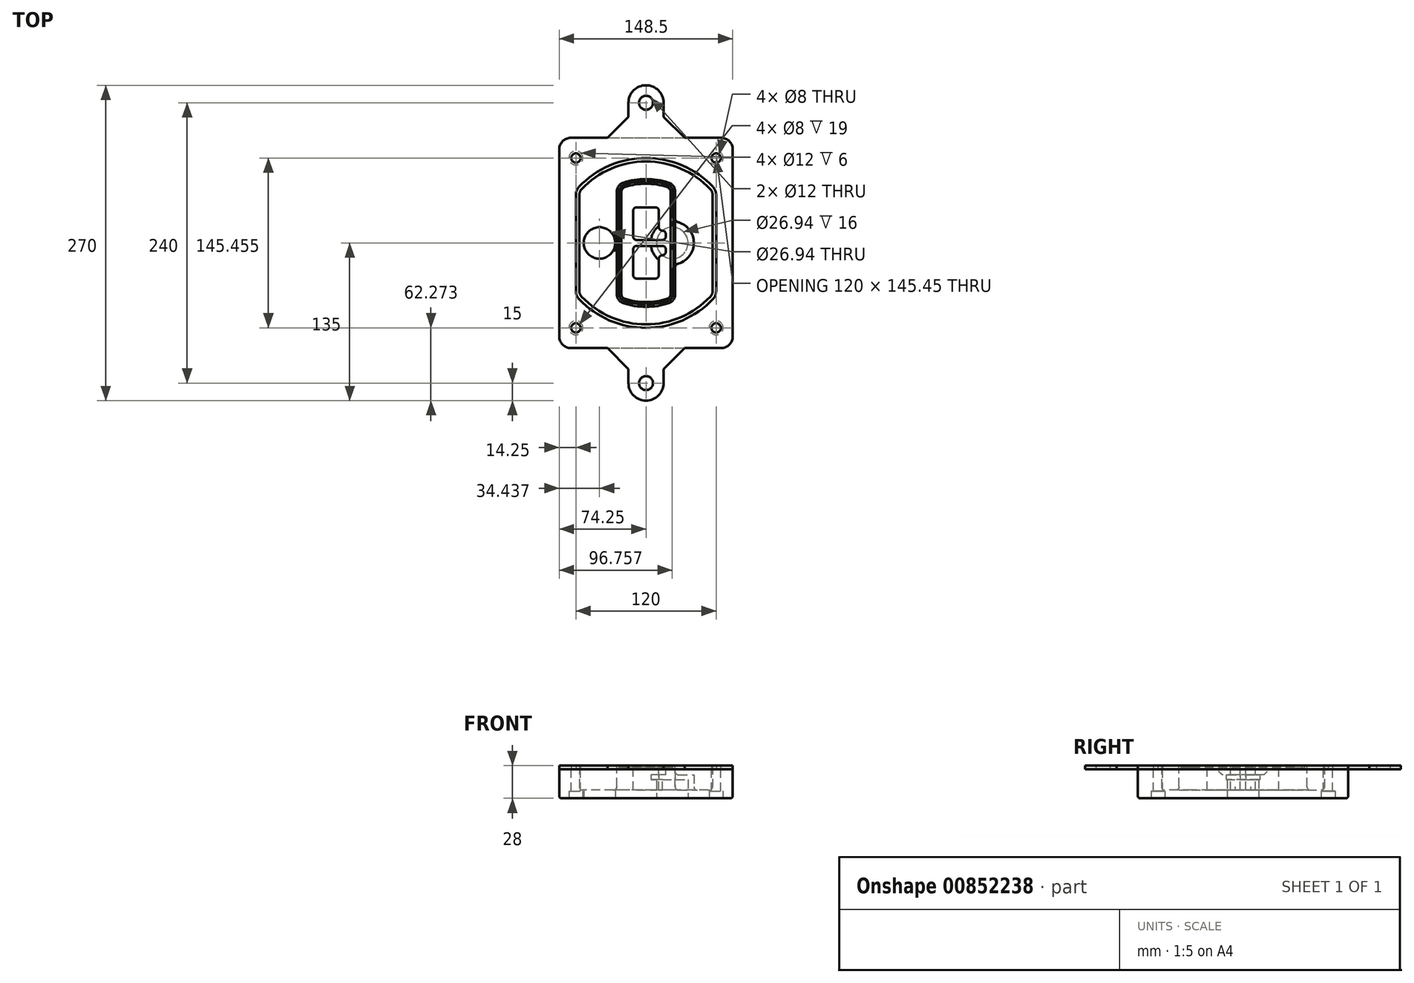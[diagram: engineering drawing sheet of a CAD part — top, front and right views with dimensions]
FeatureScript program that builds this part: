
annotation { "Feature Type Name" : "Feature", "Feature Type Description" : "" }
export const myFeature = defineFeature(function(context is Context, id is Id, definition is map)
    precondition{}
    {
        {
            var Q0;
            Q0=qCreatedBy(makeId("Top.planeOp"),FACE);
            var sketch = newSketch(context, id + "F0", { "sketchPlane" : qUnion([Q0])});
            skPoint(sketch, "E0.rect.middle", {"position": v(0, 0) * mm});
            skLineSegment(sketch, "E1.bottom", {"start": v(-64.25, -90) * mm, "end": v(64.25, -90) * mm});
            skLineSegment(sketch, "E1.top", {"start": v(-64.25, 90) * mm, "end": v(64.25, 90) * mm});
            skLineSegment(sketch, "E1.left", {"start": v(-74.25, -80) * mm, "end": v(-74.25, 80) * mm});
            skLineSegment(sketch, "E1.right", {"start": v(74.25, -80) * mm, "end": v(74.25, 80) * mm});
            skLineSegment(sketch, "E2", {"start": v(-74.25, 90) * mm, "end": v(74.25, -90) * mm, "construction": true});
            skLineSegment(sketch, "E3", {"start": v(74.25, 90) * mm, "end": v(-74.25, -90) * mm, "construction": true});
            skCircle(sketch, "E4", {"center": v(-60, 72.73) * mm, "radius": 4 * mm});
            skCircle(sketch, "E5", {"center": v(60, 72.73) * mm, "radius": 4 * mm});
            skCircle(sketch, "E6", {"center": v(60, -72.73) * mm, "radius": 4 * mm});
            skCircle(sketch, "E7", {"center": v(-60, -72.73) * mm, "radius": 4 * mm});
            skLineSegment(sketch, "E8", {"start": v(-60, 72.73) * mm, "end": v(60, 72.73) * mm, "construction": true});
            skLineSegment(sketch, "E9", {"start": v(60, 72.73) * mm, "end": v(60, -72.73) * mm, "construction": true});
            skLineSegment(sketch, "E10", {"start": v(60, -72.73) * mm, "end": v(-60, -72.73) * mm, "construction": true});
            skLineSegment(sketch, "E11", {"start": v(-60, -72.73) * mm, "end": v(-60, 72.73) * mm, "construction": true});
            skLineSegment(sketch, "E12", {"start": v(-60, 41.18) * mm, "end": v(-60, -41.18) * mm});
            skLineSegment(sketch, "E13", {"start": v(60, 41.18) * mm, "end": v(60, -41.18) * mm});
            skArc(sketch, "E14", {"start": v(57.27, 48.05) * mm, "mid": v(0, 72.73) * mm, "end": v(-57.27, 48.05) * mm});
            skArc(sketch, "E15", {"start": v(-57.27, -48.05) * mm, "mid": v(0, -72.73) * mm, "end": v(57.27, -48.05) * mm});
            skLineSegment(sketch, "E16", {"start": v(-60, 0) * mm, "end": v(60, 0) * mm, "construction": true});
            skPoint(sketch, "E17.visualSharp", {"position": v(-60, -45) * mm});
            skArc(sketch, "E17.filletArc", {"start": v(-60, -41.18) * mm, "mid": v(-59.3, -44.87) * mm, "end": v(-57.27, -48.05) * mm});
            skPoint(sketch, "E18.visualSharp", {"position": v(-60, 45) * mm});
            skArc(sketch, "E18.filletArc", {"start": v(-57.27, 48.05) * mm, "mid": v(-59.3, 44.87) * mm, "end": v(-60, 41.18) * mm});
            skPoint(sketch, "E19.visualSharp", {"position": v(60, 45) * mm});
            skArc(sketch, "E19.filletArc", {"start": v(60, 41.18) * mm, "mid": v(59.3, 44.87) * mm, "end": v(57.27, 48.05) * mm});
            skPoint(sketch, "E20.visualSharp", {"position": v(60, -45) * mm});
            skArc(sketch, "E20.filletArc", {"start": v(57.27, -48.05) * mm, "mid": v(59.3, -44.87) * mm, "end": v(60, -41.18) * mm});
            skPoint(sketch, "E21.visualSharp", {"position": v(-74.25, 90) * mm});
            skArc(sketch, "E21.filletArc", {"start": v(-64.25, 90) * mm, "mid": v(-71.32, 87.07) * mm, "end": v(-74.25, 80) * mm});
            skPoint(sketch, "E22.visualSharp", {"position": v(74.25, 90) * mm});
            skArc(sketch, "E22.filletArc", {"start": v(74.25, 80) * mm, "mid": v(71.32, 87.07) * mm, "end": v(64.25, 90) * mm});
            skPoint(sketch, "E23.visualSharp", {"position": v(74.25, -90) * mm});
            skArc(sketch, "E23.filletArc", {"start": v(64.25, -90) * mm, "mid": v(71.32, -87.07) * mm, "end": v(74.25, -80) * mm});
            skPoint(sketch, "E24.visualSharp", {"position": v(-74.25, -90) * mm});
            skArc(sketch, "E24.filletArc", {"start": v(-74.25, -80) * mm, "mid": v(-71.32, -87.07) * mm, "end": v(-64.25, -90) * mm});
            skArc(sketch, "E25.0", {"start": v(57, 41.18) * mm, "mid": v(56.5, 43.76) * mm, "end": v(55.09, 45.99) * mm});
            skLineSegment(sketch, "E25.1", {"start": v(57, 41.18) * mm, "end": v(57, -41.18) * mm});
            skArc(sketch, "E25.2", {"start": v(55.09, -45.99) * mm, "mid": v(56.5, -43.76) * mm, "end": v(57, -41.18) * mm});
            skArc(sketch, "E25.3", {"start": v(-55.09, -45.99) * mm, "mid": v(0, -69.73) * mm, "end": v(55.09, -45.99) * mm});
            skArc(sketch, "E25.4", {"start": v(-57, -41.18) * mm, "mid": v(-56.5, -43.76) * mm, "end": v(-55.09, -45.99) * mm});
            skArc(sketch, "E25.5", {"start": v(55.09, 45.99) * mm, "mid": v(0, 69.73) * mm, "end": v(-55.09, 45.99) * mm});
            skLineSegment(sketch, "E25.6", {"start": v(-57, 41.18) * mm, "end": v(-57, -41.18) * mm});
            skArc(sketch, "E25.7", {"start": v(-55.09, 45.99) * mm, "mid": v(-56.5, 43.76) * mm, "end": v(-57, 41.18) * mm});
            skArc(sketch, "E26.0", {"start": v(-60.18, 50.8) * mm, "mid": v(-63, 46.35) * mm, "end": v(-64, 41.18) * mm});
            skArc(sketch, "E26.1", {"start": v(60.18, 50.8) * mm, "mid": v(0, 76.73) * mm, "end": v(-60.18, 50.8) * mm});
            skArc(sketch, "E26.2", {"start": v(64, 41.18) * mm, "mid": v(63, 46.35) * mm, "end": v(60.18, 50.8) * mm});
            skLineSegment(sketch, "E26.3", {"start": v(64, 41.18) * mm, "end": v(64, -41.18) * mm});
            skArc(sketch, "E26.4", {"start": v(60.18, -50.8) * mm, "mid": v(63, -46.35) * mm, "end": v(64, -41.18) * mm});
            skLineSegment(sketch, "E26.5", {"start": v(-64, 41.18) * mm, "end": v(-64, -41.18) * mm});
            skArc(sketch, "E26.6", {"start": v(-60.18, -50.8) * mm, "mid": v(0, -76.73) * mm, "end": v(60.18, -50.8) * mm});
            skArc(sketch, "E26.7", {"start": v(-64, -41.18) * mm, "mid": v(-63, -46.35) * mm, "end": v(-60.18, -50.8) * mm});
            skSolve(sketch);
        }
        {
            var Q0;
            Q0=makeQuery(id+"F0.imprint","IMPRINT",FACE,{"disambiguationData":[TD([[makeQuery(id+"F0.imprint","IMPRINT",EDGE,{"derivedFrom":sQuery(id+"F0.wireOp",EDGE,"E1.bottom")}),1.0]])]});
            var Q1;
            Q1=makeQuery(id+"F0.imprint","IMPRINT",FACE,{"disambiguationData":[TD([[makeQuery(id+"F0.imprint","IMPRINT",EDGE,{"derivedFrom":sQuery(id+"F0.wireOp",EDGE,"E12")}),1.0]])]});
            var Q2;
            Q2=makeQuery(id+"F0.imprint","IMPRINT",FACE,{"disambiguationData":[TD([[makeQuery(id+"F0.imprint","IMPRINT",EDGE,{"derivedFrom":sQuery(id+"F0.wireOp",EDGE,"E25.0")}),1.0]])]});
            var Q3;
            Q3=makeQuery(id+"F0.imprint","IMPRINT",FACE,{"disambiguationData":[TD([[makeQuery(id+"F0.imprint","IMPRINT",EDGE,{"derivedFrom":sQuery(id+"F0.wireOp",EDGE,"E12")}),-1.0]])]});
            extrude(context, id + "F1", {"entities" : qUnion([Q0, Q1, Q2, Q3]), "oppositeDirection" : true, "depth" : 25 * mm});
        }
        {
            var Q0;
            Q0=makeQuery(id+"F0.imprint","IMPRINT",FACE,{"disambiguationData":[TD([[makeQuery(id+"F0.imprint","IMPRINT",EDGE,{"derivedFrom":sQuery(id+"F0.wireOp",EDGE,"E12")}),1.0]])]});
            extrude(context, id + "F2", {"entities" : qUnion([Q0]), "operationType" : NewBodyOperationType.ADD, "depth" : 3 * mm});
        }
        {
            var Q0;
            Q0=makeQuery(id+"F0.imprint","IMPRINT",FACE,{"disambiguationData":[TD([[makeQuery(id+"F0.imprint","IMPRINT",EDGE,{"derivedFrom":sQuery(id+"F0.wireOp",EDGE,"E25.0")}),1.0]])]});
            extrude(context, id + "F3", {"entities" : qUnion([Q0]), "operationType" : NewBodyOperationType.REMOVE, "oppositeDirection" : true, "depth" : 18 * mm});
        }
        {
            var Q0;
            Q0=makeQuery(id+"F2.opExtrude","CAP_FACE",FACE,{"disambiguationData":[OSD([sQuery(id+"F0.wireOp",EDGE,"E12"),sQuery(id+"F0.wireOp",EDGE,"E13"),sQuery(id+"F0.wireOp",EDGE,"E14"),sQuery(id+"F0.wireOp",EDGE,"E15"),sQuery(id+"F0.wireOp",EDGE,"E17.filletArc"),sQuery(id+"F0.wireOp",EDGE,"E18.filletArc"),sQuery(id+"F0.wireOp",EDGE,"E19.filletArc"),sQuery(id+"F0.wireOp",EDGE,"E20.filletArc"),sQuery(id+"F0.wireOp",EDGE,"E25.0"),sQuery(id+"F0.wireOp",EDGE,"E25.1"),sQuery(id+"F0.wireOp",EDGE,"E25.2"),sQuery(id+"F0.wireOp",EDGE,"E25.3"),sQuery(id+"F0.wireOp",EDGE,"E25.4"),sQuery(id+"F0.wireOp",EDGE,"E25.5"),sQuery(id+"F0.wireOp",EDGE,"E25.6"),sQuery(id+"F0.wireOp",EDGE,"E25.7")])],"isStart":false});
            var sketch = newSketch(context, id + "F4", { "sketchPlane" : qUnion([Q0])});
            skArc(sketch, "E27.0", {"start": v(-19.58, -51.49) * mm, "mid": v(0, -54.73) * mm, "end": v(19.58, -51.49) * mm});
            skArc(sketch, "E28.0", {"start": v(19.58, 51.49) * mm, "mid": v(0, 54.73) * mm, "end": v(-19.58, 51.49) * mm});
            skLineSegment(sketch, "E29", {"start": v(-25, 43.91) * mm, "end": v(-25, -43.91) * mm});
            skLineSegment(sketch, "E30", {"start": v(25, 43.91) * mm, "end": v(25, -43.91) * mm});
            skLineSegment(sketch, "E31", {"start": v(-25, 49.35) * mm, "end": v(25, 49.35) * mm, "construction": true});
            skLineSegment(sketch, "E32", {"start": v(-25, -49.35) * mm, "end": v(25, -49.35) * mm, "construction": true});
            skPoint(sketch, "E33.visualSharp", {"position": v(-25, 49.35) * mm});
            skArc(sketch, "E33.filletArc", {"start": v(-19.58, 51.49) * mm, "mid": v(-23.5, 48.57) * mm, "end": v(-25, 43.91) * mm});
            skPoint(sketch, "E34.visualSharp", {"position": v(25, 49.35) * mm});
            skArc(sketch, "E34.filletArc", {"start": v(25, 43.91) * mm, "mid": v(23.5, 48.57) * mm, "end": v(19.58, 51.49) * mm});
            skPoint(sketch, "E35.visualSharp", {"position": v(25, -49.35) * mm});
            skArc(sketch, "E35.filletArc", {"start": v(19.58, -51.49) * mm, "mid": v(23.5, -48.57) * mm, "end": v(25, -43.91) * mm});
            skPoint(sketch, "E36.visualSharp", {"position": v(-25, -49.35) * mm});
            skArc(sketch, "E36.filletArc", {"start": v(-25, -43.91) * mm, "mid": v(-23.5, -48.57) * mm, "end": v(-19.58, -51.49) * mm});
            skArc(sketch, "E37.0", {"start": v(55.09, 45.99) * mm, "mid": v(0, 69.73) * mm, "end": v(-55.09, 45.99) * mm});
            skArc(sketch, "E37.1", {"start": v(-55.09, 45.99) * mm, "mid": v(-56.5, 43.76) * mm, "end": v(-57, 41.18) * mm});
            skLineSegment(sketch, "E37.2", {"start": v(-57, 41.18) * mm, "end": v(-57, -41.18) * mm});
            skArc(sketch, "E37.3", {"start": v(-57, -41.18) * mm, "mid": v(-56.5, -43.76) * mm, "end": v(-55.09, -45.99) * mm});
            skArc(sketch, "E37.4", {"start": v(-55.09, -45.99) * mm, "mid": v(0, -69.73) * mm, "end": v(55.09, -45.99) * mm});
            skArc(sketch, "E37.5", {"start": v(55.09, -45.99) * mm, "mid": v(56.5, -43.76) * mm, "end": v(57, -41.18) * mm});
            skLineSegment(sketch, "E37.6", {"start": v(57, 41.18) * mm, "end": v(57, -41.18) * mm});
            skArc(sketch, "E37.7", {"start": v(57, 41.18) * mm, "mid": v(56.5, 43.76) * mm, "end": v(55.09, 45.99) * mm});
            skLineSegment(sketch, "E38.0", {"start": v(23, 43.91) * mm, "end": v(23, -43.91) * mm});
            skArc(sketch, "E38.1", {"start": v(18.93, -49.6) * mm, "mid": v(21.88, -47.4) * mm, "end": v(23, -43.91) * mm});
            skArc(sketch, "E38.2", {"start": v(-18.93, -49.6) * mm, "mid": v(0, -52.73) * mm, "end": v(18.93, -49.6) * mm});
            skArc(sketch, "E38.3", {"start": v(-23, -43.91) * mm, "mid": v(-21.88, -47.4) * mm, "end": v(-18.93, -49.6) * mm});
            skLineSegment(sketch, "E38.4", {"start": v(-23, 43.91) * mm, "end": v(-23, -43.91) * mm});
            skArc(sketch, "E38.5", {"start": v(23, 43.91) * mm, "mid": v(21.88, 47.4) * mm, "end": v(18.93, 49.6) * mm});
            skArc(sketch, "E38.6", {"start": v(-18.93, 49.6) * mm, "mid": v(-21.88, 47.4) * mm, "end": v(-23, 43.91) * mm});
            skArc(sketch, "E38.7", {"start": v(18.93, 49.6) * mm, "mid": v(0, 52.73) * mm, "end": v(-18.93, 49.6) * mm});
            skArc(sketch, "E39.0", {"start": v(21, 43.91) * mm, "mid": v(20.25, 46.24) * mm, "end": v(18.29, 47.7) * mm});
            skLineSegment(sketch, "E39.1", {"start": v(21, 43.91) * mm, "end": v(21, -43.91) * mm});
            skArc(sketch, "E39.2", {"start": v(18.29, -47.7) * mm, "mid": v(20.25, -46.24) * mm, "end": v(21, -43.91) * mm});
            skArc(sketch, "E39.3", {"start": v(-18.29, -47.7) * mm, "mid": v(0, -50.73) * mm, "end": v(18.29, -47.7) * mm});
            skArc(sketch, "E39.4", {"start": v(-21, -43.91) * mm, "mid": v(-20.25, -46.24) * mm, "end": v(-18.29, -47.7) * mm});
            skArc(sketch, "E39.5", {"start": v(18.29, 47.7) * mm, "mid": v(0, 50.73) * mm, "end": v(-18.29, 47.7) * mm});
            skLineSegment(sketch, "E39.6", {"start": v(-21, 43.91) * mm, "end": v(-21, -43.91) * mm});
            skArc(sketch, "E39.7", {"start": v(-18.29, 47.7) * mm, "mid": v(-20.25, 46.24) * mm, "end": v(-21, 43.91) * mm});
            skLineSegment(sketch, "E40", {"start": v(-25, 0) * mm, "end": v(25, 0) * mm, "construction": true});
            skLineSegment(sketch, "E41", {"start": v(-11, 5.5) * mm, "end": v(-11, 27.5) * mm});
            skLineSegment(sketch, "E42", {"start": v(-8, 30.5) * mm, "end": v(8, 30.5) * mm});
            skLineSegment(sketch, "E43", {"start": v(11, 27.5) * mm, "end": v(11, 13.5) * mm});
            skLineSegment(sketch, "E44", {"start": v(14, 10.5) * mm, "end": v(14, 10.5) * mm});
            skLineSegment(sketch, "E45", {"start": v(17, 7.5) * mm, "end": v(17, 5.5) * mm});
            skLineSegment(sketch, "E46", {"start": v(14, 2.5) * mm, "end": v(-8, 2.5) * mm});
            skPoint(sketch, "E47.visualSharp", {"position": v(-11, 30.5) * mm});
            skArc(sketch, "E47.filletArc", {"start": v(-8, 30.5) * mm, "mid": v(-10.12, 29.62) * mm, "end": v(-11, 27.5) * mm});
            skPoint(sketch, "E48.visualSharp", {"position": v(11, 30.5) * mm});
            skArc(sketch, "E48.filletArc", {"start": v(11, 27.5) * mm, "mid": v(10.12, 29.62) * mm, "end": v(8, 30.5) * mm});
            skPoint(sketch, "E49.visualSharp", {"position": v(11, 10.5) * mm});
            skArc(sketch, "E49.filletArc", {"start": v(11, 13.5) * mm, "mid": v(11.88, 11.38) * mm, "end": v(14, 10.5) * mm});
            skPoint(sketch, "E50.visualSharp", {"position": v(17, 10.5) * mm});
            skArc(sketch, "E50.filletArc", {"start": v(17, 7.5) * mm, "mid": v(16.12, 9.62) * mm, "end": v(14, 10.5) * mm});
            skPoint(sketch, "E51.visualSharp", {"position": v(17, 2.5) * mm});
            skArc(sketch, "E51.filletArc", {"start": v(14, 2.5) * mm, "mid": v(16.12, 3.38) * mm, "end": v(17, 5.5) * mm});
            skPoint(sketch, "E52.visualSharp", {"position": v(-11, 2.5) * mm});
            skArc(sketch, "E52.filletArc", {"start": v(-11, 5.5) * mm, "mid": v(-10.12, 3.38) * mm, "end": v(-8, 2.5) * mm});
            skLineSegment(sketch, "E53.0.MirrorCS", {"start": v(14, -2.5) * mm, "end": v(-8, -2.5) * mm});
            skArc(sketch, "E54.0.MirrorCS", {"start": v(-11, -5.5) * mm, "mid": v(-10.12, -3.38) * mm, "end": v(-8, -2.5) * mm});
            skLineSegment(sketch, "E55.0.MirrorCS", {"start": v(-11, -5.5) * mm, "end": v(-11, -27.5) * mm});
            skArc(sketch, "E56.0.MirrorCS", {"start": v(-8, -30.5) * mm, "mid": v(-10.12, -29.62) * mm, "end": v(-11, -27.5) * mm});
            skLineSegment(sketch, "E57.0.MirrorCS", {"start": v(-8, -30.5) * mm, "end": v(8, -30.5) * mm});
            skArc(sketch, "E58.0.MirrorCS", {"start": v(11, -27.5) * mm, "mid": v(10.12, -29.62) * mm, "end": v(8, -30.5) * mm});
            skLineSegment(sketch, "E59.0.MirrorCS", {"start": v(11, -27.5) * mm, "end": v(11, -13.5) * mm});
            skArc(sketch, "E60.0.MirrorCS", {"start": v(11, -13.5) * mm, "mid": v(11.88, -11.38) * mm, "end": v(14, -10.5) * mm});
            skArc(sketch, "E61.0.MirrorCS", {"start": v(17, -7.5) * mm, "mid": v(16.12, -9.62) * mm, "end": v(14, -10.5) * mm});
            skLineSegment(sketch, "E62.0.MirrorCS", {"start": v(17, -7.5) * mm, "end": v(17, -5.5) * mm});
            skArc(sketch, "E63.0.MirrorCS", {"start": v(14, -2.5) * mm, "mid": v(16.12, -3.38) * mm, "end": v(17, -5.5) * mm});
            skSolve(sketch);
        }
        {
            var Q0;
            Q0=makeQuery(id+"F4.imprint","IMPRINT",FACE,{"disambiguationData":[TD([[makeQuery(id+"F4.imprint","IMPRINT",EDGE,{"derivedFrom":sQuery(id+"F4.wireOp",EDGE,"E27.0")}),1.0]])]});
            var Q1;
            Q1=makeQuery(id+"F4.imprint","IMPRINT",FACE,{"disambiguationData":[TD([[makeQuery(id+"F4.imprint","IMPRINT",EDGE,{"derivedFrom":sQuery(id+"F4.wireOp",EDGE,"E38.0")}),-1.0]])]});
            var Q2;
            Q2=makeQuery(id+"F4.imprint","IMPRINT",FACE,{"disambiguationData":[TD([[makeQuery(id+"F4.imprint","IMPRINT",EDGE,{"derivedFrom":sQuery(id+"F4.wireOp",EDGE,"E39.0")}),1.0]])]});
            extrude(context, id + "F5", {"entities" : qUnion([Q0, Q1, Q2]), "operationType" : NewBodyOperationType.ADD, "endBound" : BoundingType.UP_TO_NEXT, "oppositeDirection" : true, "depth" : 25 * mm});
        }
        {
            var Q0;
            Q0=makeQuery(id+"F4.imprint","IMPRINT",FACE,{"disambiguationData":[TD([[makeQuery(id+"F4.imprint","IMPRINT",EDGE,{"derivedFrom":sQuery(id+"F4.wireOp",EDGE,"E38.0")}),-1.0]])]});
            extrude(context, id + "F6", {"entities" : qUnion([Q0]), "operationType" : NewBodyOperationType.REMOVE, "oppositeDirection" : true, "depth" : 2 * mm});
        }
        {
            var Q0;
            Q0=makeQuery(id+"F1.opExtrude","CAP_FACE",FACE,{"disambiguationData":[OSD([sQuery(id+"F0.wireOp",EDGE,"E1.bottom"),sQuery(id+"F0.wireOp",EDGE,"E1.top"),sQuery(id+"F0.wireOp",EDGE,"E1.left"),sQuery(id+"F0.wireOp",EDGE,"E1.right"),sQuery(id+"F0.wireOp",EDGE,"E4"),sQuery(id+"F0.wireOp",EDGE,"E5"),sQuery(id+"F0.wireOp",EDGE,"E6"),sQuery(id+"F0.wireOp",EDGE,"E7"),sQuery(id+"F0.wireOp",EDGE,"E21.filletArc"),sQuery(id+"F0.wireOp",EDGE,"E22.filletArc"),sQuery(id+"F0.wireOp",EDGE,"E23.filletArc"),sQuery(id+"F0.wireOp",EDGE,"E24.filletArc")])],"isStart":false});
            var sketch = newSketch(context, id + "F7", { "sketchPlane" : qUnion([Q0])});
            skCircle(sketch, "E64", {"center": v(22.5, 0) * mm, "radius": 13.47 * mm});
            skCircle(sketch, "E65", {"center": v(-39.81, 0) * mm, "radius": 13.47 * mm});
            skLineSegment(sketch, "E66", {"start": v(74.25, 0) * mm, "end": v(-74.25, 0) * mm});
            skCircle(sketch, "E67", {"center": v(22.5, 0) * mm, "radius": 18.47 * mm});
            skCircle(sketch, "E68", {"center": v(60, -72.73) * mm, "radius": 6 * mm});
            skCircle(sketch, "E69", {"center": v(-60, -72.73) * mm, "radius": 6 * mm});
            skCircle(sketch, "E70", {"center": v(-60, 72.73) * mm, "radius": 6 * mm});
            skCircle(sketch, "E71", {"center": v(60, 72.73) * mm, "radius": 6 * mm});
            skSolve(sketch);
        }
        {
            var Q0;
            {var subQ1=sQuery(id+"F7.wireOp",EDGE,"E66");var subQ4=sQuery(id+"F7.wireOp",EDGE,"E64");var subQ6=makeQuery(id+"F7.imprint","INTERSECT",VERTEX,{"disambiguationData":[OD(0.0)],"derivedFrom":[subQ4,subQ1]});Q0=makeQuery(id+"F7.imprint","IMPRINT",FACE,{"disambiguationData":[TD([[makeQuery(id+"F7.imprint","IMPRINT",EDGE,{"disambiguationData":[TD([[subQ6,-1.0]])],"derivedFrom":subQ4}),-1.0]])]});}
            var Q1;
            {var subQ0=sQuery(id+"F7.wireOp",EDGE,"E66");var subQ1=sQuery(id+"F7.wireOp",EDGE,"E64");var subQ3=makeQuery(id+"F7.imprint","INTERSECT",VERTEX,{"disambiguationData":[OD(0.0)],"derivedFrom":[subQ1,subQ0]});Q1=makeQuery(id+"F7.imprint","IMPRINT",FACE,{"disambiguationData":[TD([[makeQuery(id+"F7.imprint","IMPRINT",EDGE,{"disambiguationData":[TD([[subQ3,-1.0]])],"derivedFrom":subQ1}),1.0]])]});}
            var Q2;
            {var subQ0=sQuery(id+"F7.wireOp",EDGE,"E66");var subQ1=sQuery(id+"F7.wireOp",EDGE,"E64");var subQ3=makeQuery(id+"F7.imprint","INTERSECT",VERTEX,{"disambiguationData":[OD(0.0)],"derivedFrom":[subQ1,subQ0]});Q2=makeQuery(id+"F7.imprint","IMPRINT",FACE,{"disambiguationData":[TD([[makeQuery(id+"F7.imprint","IMPRINT",EDGE,{"disambiguationData":[TD([[subQ3,1.0]])],"derivedFrom":subQ1}),1.0]])]});}
            var Q3;
            {var subQ1=sQuery(id+"F7.wireOp",EDGE,"E66");var subQ4=sQuery(id+"F7.wireOp",EDGE,"E64");var subQ6=makeQuery(id+"F7.imprint","INTERSECT",VERTEX,{"disambiguationData":[OD(0.0)],"derivedFrom":[subQ4,subQ1]});Q3=makeQuery(id+"F7.imprint","IMPRINT",FACE,{"disambiguationData":[TD([[makeQuery(id+"F7.imprint","IMPRINT",EDGE,{"disambiguationData":[TD([[subQ6,1.0]])],"derivedFrom":subQ4}),-1.0]])]});}
            extrude(context, id + "F8", {"entities" : qUnion([Q0, Q1, Q2, Q3]), "operationType" : NewBodyOperationType.ADD, "oppositeDirection" : true, "depth" : 20 * mm});
        }
        {
            var Q0;
            {var subQ0=sQuery(id+"F7.wireOp",EDGE,"E66");var subQ1=sQuery(id+"F7.wireOp",EDGE,"E64");var subQ3=makeQuery(id+"F7.imprint","INTERSECT",VERTEX,{"disambiguationData":[OD(0.0)],"derivedFrom":[subQ1,subQ0]});Q0=makeQuery(id+"F7.imprint","IMPRINT",FACE,{"disambiguationData":[TD([[makeQuery(id+"F7.imprint","IMPRINT",EDGE,{"disambiguationData":[TD([[subQ3,-1.0]])],"derivedFrom":subQ1}),1.0]])]});}
            var Q1;
            {var subQ0=sQuery(id+"F7.wireOp",EDGE,"E66");var subQ1=sQuery(id+"F7.wireOp",EDGE,"E64");var subQ3=makeQuery(id+"F7.imprint","INTERSECT",VERTEX,{"disambiguationData":[OD(0.0)],"derivedFrom":[subQ1,subQ0]});Q1=makeQuery(id+"F7.imprint","IMPRINT",FACE,{"disambiguationData":[TD([[makeQuery(id+"F7.imprint","IMPRINT",EDGE,{"disambiguationData":[TD([[subQ3,1.0]])],"derivedFrom":subQ1}),1.0]])]});}
            extrude(context, id + "F9", {"entities" : qUnion([Q0, Q1]), "operationType" : NewBodyOperationType.REMOVE, "oppositeDirection" : true, "depth" : 16 * mm});
        }
        {
            var Q0;
            {var subQ0=sQuery(id+"F7.wireOp",EDGE,"E66");var subQ1=sQuery(id+"F7.wireOp",EDGE,"E65");var subQ3=makeQuery(id+"F7.imprint","INTERSECT",VERTEX,{"disambiguationData":[OD(0.0)],"derivedFrom":[subQ1,subQ0]});Q0=makeQuery(id+"F7.imprint","IMPRINT",FACE,{"disambiguationData":[TD([[makeQuery(id+"F7.imprint","IMPRINT",EDGE,{"disambiguationData":[TD([[subQ3,-1.0]])],"derivedFrom":subQ1}),1.0]])]});}
            var Q1;
            {var subQ0=sQuery(id+"F7.wireOp",EDGE,"E66");var subQ1=sQuery(id+"F7.wireOp",EDGE,"E65");var subQ3=makeQuery(id+"F7.imprint","INTERSECT",VERTEX,{"disambiguationData":[OD(0.0)],"derivedFrom":[subQ1,subQ0]});Q1=makeQuery(id+"F7.imprint","IMPRINT",FACE,{"disambiguationData":[TD([[makeQuery(id+"F7.imprint","IMPRINT",EDGE,{"disambiguationData":[TD([[subQ3,1.0]])],"derivedFrom":subQ1}),1.0]])]});}
            extrude(context, id + "F10", {"entities" : qUnion([Q0, Q1]), "operationType" : NewBodyOperationType.REMOVE, "oppositeDirection" : true, "depth" : 25 * mm});
        }
        {
            var Q0;
            Q0=makeQuery(id+"F7.imprint","IMPRINT",FACE,{"disambiguationData":[TD([[makeQuery(id+"F7.imprint","IMPRINT",EDGE,{"derivedFrom":sQuery(id+"F7.wireOp",EDGE,"E68")}),1.0]])]});
            var Q1;
            Q1=makeQuery(id+"F7.imprint","IMPRINT",FACE,{"disambiguationData":[TD([[makeQuery(id+"F7.imprint","IMPRINT",EDGE,{"derivedFrom":makeQuery(id+"F1.opExtrude","CAP_EDGE",EDGE,{"disambiguationData":[OSD([sQuery(id+"F0.wireOp",EDGE,"E5")])],"isStart":false})}),-1.0]])]});
            var Q2;
            Q2=makeQuery(id+"F7.imprint","IMPRINT",FACE,{"disambiguationData":[TD([[makeQuery(id+"F7.imprint","IMPRINT",EDGE,{"derivedFrom":sQuery(id+"F7.wireOp",EDGE,"E69")}),1.0]])]});
            var Q3;
            Q3=makeQuery(id+"F7.imprint","IMPRINT",FACE,{"disambiguationData":[TD([[makeQuery(id+"F7.imprint","IMPRINT",EDGE,{"derivedFrom":makeQuery(id+"F1.opExtrude","CAP_EDGE",EDGE,{"disambiguationData":[OSD([sQuery(id+"F0.wireOp",EDGE,"E4")])],"isStart":false})}),-1.0]])]});
            var Q4;
            Q4=makeQuery(id+"F7.imprint","IMPRINT",FACE,{"disambiguationData":[TD([[makeQuery(id+"F7.imprint","IMPRINT",EDGE,{"derivedFrom":sQuery(id+"F7.wireOp",EDGE,"E70")}),1.0]])]});
            var Q5;
            Q5=makeQuery(id+"F7.imprint","IMPRINT",FACE,{"disambiguationData":[TD([[makeQuery(id+"F7.imprint","IMPRINT",EDGE,{"derivedFrom":makeQuery(id+"F1.opExtrude","CAP_EDGE",EDGE,{"disambiguationData":[OSD([sQuery(id+"F0.wireOp",EDGE,"E7")])],"isStart":false})}),-1.0]])]});
            var Q6;
            Q6=makeQuery(id+"F7.imprint","IMPRINT",FACE,{"disambiguationData":[TD([[makeQuery(id+"F7.imprint","IMPRINT",EDGE,{"derivedFrom":sQuery(id+"F7.wireOp",EDGE,"E71")}),1.0]])]});
            var Q7;
            Q7=makeQuery(id+"F7.imprint","IMPRINT",FACE,{"disambiguationData":[TD([[makeQuery(id+"F7.imprint","IMPRINT",EDGE,{"derivedFrom":makeQuery(id+"F1.opExtrude","CAP_EDGE",EDGE,{"disambiguationData":[OSD([sQuery(id+"F0.wireOp",EDGE,"E6")])],"isStart":false})}),-1.0]])]});
            extrude(context, id + "F11", {"entities" : qUnion([Q0, Q1, Q2, Q3, Q4, Q5, Q6, Q7]), "operationType" : NewBodyOperationType.REMOVE, "oppositeDirection" : true, "depth" : 6 * mm});
        }
        {
            var Q0;
            Q0=makeQuery(id+"F9.boolean.opBoolean","COPY",FACE,{"derivedFrom":makeQuery(id+"F9.opExtrude","CAP_FACE",FACE,{"disambiguationData":[OSD([sQuery(id+"F7.wireOp",EDGE,"E64")])],"isStart":false})});
            var sketch = newSketch(context, id + "F12", { "sketchPlane" : qUnion([Q0])});
            skArc(sketch, "E72.0", {"start": v(11, 14.45) * mm, "mid": v(6.45, 9.13) * mm, "end": v(4.2, 2.5) * mm});
            skArc(sketch, "E72.1", {"start": v(4.2, -2.5) * mm, "mid": v(6.45, -9.13) * mm, "end": v(11, -14.45) * mm});
            skLineSegment(sketch, "E73", {"start": v(4.2, -2.5) * mm, "end": v(14, -2.5) * mm});
            skLineSegment(sketch, "E74.0", {"start": v(14, 2.5) * mm, "end": v(4.2, 2.5) * mm});
            skArc(sketch, "E74.1", {"start": v(14, 2.5) * mm, "mid": v(16.12, 3.38) * mm, "end": v(17, 5.5) * mm});
            skLineSegment(sketch, "E74.2", {"start": v(17, 7.5) * mm, "end": v(17, 5.5) * mm});
            skArc(sketch, "E74.3", {"start": v(17, 7.5) * mm, "mid": v(16.12, 9.62) * mm, "end": v(14, 10.5) * mm});
            skArc(sketch, "E74.4", {"start": v(11, 13.5) * mm, "mid": v(11.88, 11.38) * mm, "end": v(14, 10.5) * mm});
            skLineSegment(sketch, "E74.5", {"start": v(11, 14.45) * mm, "end": v(11, 13.5) * mm});
            skLineSegment(sketch, "E74.7", {"start": v(14, -2.5) * mm, "end": v(4.2, -2.5) * mm});
            skArc(sketch, "E74.8", {"start": v(14, -2.5) * mm, "mid": v(16.12, -3.38) * mm, "end": v(17, -5.5) * mm});
            skLineSegment(sketch, "E74.9", {"start": v(17, -7.5) * mm, "end": v(17, -5.5) * mm});
            skArc(sketch, "E74.10", {"start": v(17, -7.5) * mm, "mid": v(16.12, -9.62) * mm, "end": v(14, -10.5) * mm});
            skArc(sketch, "E74.11", {"start": v(11, -13.5) * mm, "mid": v(11.88, -11.38) * mm, "end": v(14, -10.5) * mm});
            skLineSegment(sketch, "E74.12", {"start": v(11, -14.45) * mm, "end": v(11, -13.5) * mm});
            skPoint(sketch, "E75.orphan", {"position": v(11, -27.5) * mm});
            skPoint(sketch, "E76.orphan", {"position": v(-8, -2.5) * mm});
            skPoint(sketch, "E77.orphan", {"position": v(-8, 2.5) * mm});
            skPoint(sketch, "E78.orphan", {"position": v(11, 27.5) * mm});
            skSolve(sketch);
        }
        {
            var Q0;
            {var subQ7=sQuery(id+"F12.wireOp",EDGE,"E72.0");var subQ14=sQuery(id+"F12.wireOp",EDGE,"E72.1");var subQ16=sQuery(id+"F12.wireOp",EDGE,"E74.1");var subQ18=sQuery(id+"F12.wireOp",EDGE,"E74.8");Q0=qUnion([makeQuery(id+"F12.imprint","IMPRINT",FACE,{"disambiguationData":[TD([[makeQuery(id+"F12.imprint","IMPRINT",EDGE,{"derivedFrom":subQ7}),1.0]])]}),makeQuery(id+"F12.imprint","IMPRINT",FACE,{"disambiguationData":[TD([[makeQuery(id+"F12.imprint","IMPRINT",EDGE,{"derivedFrom":subQ14}),1.0]])]}),makeQuery(id+"F12.imprint","IMPRINT",FACE,{"disambiguationData":[TD([[makeQuery(id+"F12.imprint","IMPRINT",EDGE,{"derivedFrom":subQ16}),1.0]])]}),makeQuery(id+"F12.imprint","IMPRINT",FACE,{"disambiguationData":[TD([[makeQuery(id+"F12.imprint","IMPRINT",EDGE,{"derivedFrom":subQ18}),-1.0]])]})]);}
            var Q1;
            Q1=makeQuery(id+"F5.boolean.opBoolean","SPLIT",FACE,{"disambiguationData":[TD([makeQuery(id+"F5.opExtrude","SWEPT_FACE",FACE,{"disambiguationData":[OSD([sQuery(id+"F4.wireOp",EDGE,"E41")])]})])],"derivedFrom":makeQuery(id+"F3.boolean.opBoolean","COPY",FACE,{"derivedFrom":makeQuery(id+"F3.opExtrude","CAP_FACE",FACE,{"disambiguationData":[OSD([sQuery(id+"F0.wireOp",EDGE,"E25.0"),sQuery(id+"F0.wireOp",EDGE,"E25.1"),sQuery(id+"F0.wireOp",EDGE,"E25.2"),sQuery(id+"F0.wireOp",EDGE,"E25.3"),sQuery(id+"F0.wireOp",EDGE,"E25.4"),sQuery(id+"F0.wireOp",EDGE,"E25.5"),sQuery(id+"F0.wireOp",EDGE,"E25.6"),sQuery(id+"F0.wireOp",EDGE,"E25.7")])],"isStart":false})})});
            extrude(context, id + "F13", {"entities" : qUnion([Q0]), "operationType" : NewBodyOperationType.REMOVE, "endBound" : BoundingType.UP_TO_SURFACE, "endBoundEntityFace" : qUnion([Q1]), "depth" : 25 * mm});
        }
        {
            var Q0;
            Q0=makeQuery(id+"F3.boolean.opBoolean","COPY",EDGE,{"derivedFrom":makeQuery(id+"F3.opExtrude","CAP_EDGE",EDGE,{"disambiguationData":[OSD([sQuery(id+"F0.wireOp",EDGE,"E25.6")])],"isStart":false})});
            var Q1;
            Q1=makeQuery(id+"F8.boolean.opBoolean","INTERSECT",EDGE,{"derivedFrom":[makeQuery(id+"F5.opExtrude","SWEPT_FACE",FACE,{"disambiguationData":[OSD([sQuery(id+"F4.wireOp",EDGE,"E30")])]}),makeQuery(id+"F8.opExtrude","CAP_FACE",FACE,{"disambiguationData":[OSD([sQuery(id+"F7.wireOp",EDGE,"E67")])],"isStart":false})]});
            var Q2;
            Q2=makeQuery(id+"F8.boolean.opBoolean","INTERSECT",EDGE,{"disambiguationData":[OD(1.0)],"derivedFrom":[makeQuery(id+"F5.opExtrude","SWEPT_FACE",FACE,{"disambiguationData":[OSD([sQuery(id+"F4.wireOp",EDGE,"E30")])]}),makeQuery(id+"F8.opExtrude","SWEPT_FACE",FACE,{"disambiguationData":[OSD([sQuery(id+"F7.wireOp",EDGE,"E67")])]})]});
            var Q3;
            {var subQ0=sQuery(id+"F4.wireOp",EDGE,"E30");Q3=makeQuery(id+"F8.boolean.opBoolean","SPLIT",EDGE,{"disambiguationData":[TD([makeQuery(id+"F5.opExtrude","SWEPT_FACE",FACE,{"disambiguationData":[OSD([sQuery(id+"F4.wireOp",EDGE,"E35.filletArc")])]})])],"derivedFrom":makeQuery(id+"F5.opExtrude","CAP_EDGE",EDGE,{"disambiguationData":[OSD([subQ0])],"isStart":false})});}
            var Q4;
            {var subQ0=sQuery(id+"F0.wireOp",EDGE,"E25.7");var subQ1=sQuery(id+"F0.wireOp",EDGE,"E25.1");var subQ2=sQuery(id+"F0.wireOp",EDGE,"E25.6");var subQ3=sQuery(id+"F0.wireOp",EDGE,"E25.5");var subQ4=sQuery(id+"F0.wireOp",EDGE,"E25.4");var subQ5=sQuery(id+"F0.wireOp",EDGE,"E25.0");var subQ6=sQuery(id+"F0.wireOp",EDGE,"E25.2");var subQ7=sQuery(id+"F0.wireOp",EDGE,"E25.3");Q4=makeQuery(id+"F8.boolean.opBoolean","INTERSECT",EDGE,{"derivedFrom":[makeQuery(id+"F5.boolean.opBoolean","SPLIT",FACE,{"disambiguationData":[TD([makeQuery(id+"F2.opExtrude","SWEPT_FACE",FACE,{"disambiguationData":[OSD([subQ5])]})])],"derivedFrom":makeQuery(id+"F3.boolean.opBoolean","COPY",FACE,{"derivedFrom":makeQuery(id+"F3.opExtrude","CAP_FACE",FACE,{"disambiguationData":[OSD([subQ5,subQ1,subQ6,subQ7,subQ4,subQ3,subQ2,subQ0])],"isStart":false})})}),makeQuery(id+"F8.opExtrude","SWEPT_FACE",FACE,{"disambiguationData":[OSD([sQuery(id+"F7.wireOp",EDGE,"E67")])]})]});}
            var Q5;
            Q5=makeQuery(id+"F8.boolean.opBoolean","INTERSECT",EDGE,{"disambiguationData":[OD(0.0)],"derivedFrom":[makeQuery(id+"F5.opExtrude","SWEPT_FACE",FACE,{"disambiguationData":[OSD([sQuery(id+"F4.wireOp",EDGE,"E30")])]}),makeQuery(id+"F8.opExtrude","SWEPT_FACE",FACE,{"disambiguationData":[OSD([sQuery(id+"F7.wireOp",EDGE,"E67")])]})]});
            fillet(context, id + "F14", {"entities" : qUnion([Q0, Q1, Q2, Q3, Q4, Q5]), "radius" : 3 * mm, "tangentPropagation" : true, "allowEdgeOverflow" : false});
        }
        {
            var Q0;
            Q0=makeQuery(id+"F1.opExtrude","CAP_EDGE",EDGE,{"disambiguationData":[OSD([sQuery(id+"F0.wireOp",EDGE,"E1.bottom")])],"isStart":false});
            fillet(context, id + "F15", {"entities" : qUnion([Q0]), "radius" : 2 * mm, "tangentPropagation" : true, "allowEdgeOverflow" : false});
        }
        {
            var Q0;
            {var subQ0=sQuery(id+"F0.wireOp",EDGE,"E21.filletArc");var subQ1=sQuery(id+"F0.wireOp",EDGE,"E7");var subQ2=sQuery(id+"F0.wireOp",EDGE,"E6");var subQ3=sQuery(id+"F0.wireOp",EDGE,"E5");var subQ4=sQuery(id+"F0.wireOp",EDGE,"E4");var subQ5=sQuery(id+"F0.wireOp",EDGE,"E22.filletArc");var subQ6=sQuery(id+"F0.wireOp",EDGE,"E1.bottom");var subQ7=sQuery(id+"F0.wireOp",EDGE,"E1.right");var subQ8=sQuery(id+"F0.wireOp",EDGE,"E1.top");var subQ9=sQuery(id+"F0.wireOp",EDGE,"E1.left");var subQ10=sQuery(id+"F0.wireOp",EDGE,"E23.filletArc");var subQ11=sQuery(id+"F0.wireOp",EDGE,"E24.filletArc");Q0=makeQuery(id+"F2.boolean.opBoolean","SPLIT",FACE,{"disambiguationData":[TD([makeQuery(id+"F1.opExtrude","SWEPT_FACE",FACE,{"disambiguationData":[OSD([subQ6])]})])],"derivedFrom":makeQuery(id+"F1.opExtrude","CAP_FACE",FACE,{"disambiguationData":[OSD([subQ6,subQ8,subQ9,subQ7,subQ4,subQ3,subQ2,subQ1,subQ0,subQ5,subQ10,subQ11])],"isStart":true})});}
            var sketch = newSketch(context, id + "F16", { "sketchPlane" : qUnion([Q0])});
            skLineSegment(sketch, "E79", {"start": v(0, 0) * mm, "end": v(0, 120) * mm, "construction": true});
            skPoint(sketch, "E79.endSnap0", {"position": v(0, 90) * mm});
            skCircle(sketch, "E80", {"center": v(0, 120) * mm, "radius": 6 * mm});
            skArc(sketch, "E81", {"start": v(15, 120) * mm, "mid": v(0, 135) * mm, "end": v(-15, 120) * mm});
            skLineSegment(sketch, "E82", {"start": v(-33, 90) * mm, "end": v(-15, 108) * mm});
            skLineSegment(sketch, "E83", {"start": v(-15, 108) * mm, "end": v(-15, 120) * mm});
            skLineSegment(sketch, "E84", {"start": v(-33, 90) * mm, "end": v(33, 90) * mm});
            skLineSegment(sketch, "E85", {"start": v(15, 120) * mm, "end": v(15, 108) * mm});
            skLineSegment(sketch, "E86", {"start": v(15, 108) * mm, "end": v(33, 90) * mm});
            skPoint(sketch, "E87.end.orphan", {"position": v(-74.25, 0) * mm});
            skLineSegment(sketch, "E88", {"start": v(-74.25, 0) * mm, "end": v(74.25, 0) * mm, "construction": true});
            skLineSegment(sketch, "E89.MirrorCS", {"start": v(15, -120) * mm, "end": v(15, -108) * mm});
            skLineSegment(sketch, "E90.MirrorCS", {"start": v(-15, -108) * mm, "end": v(-15, -120) * mm});
            skPoint(sketch, "E91.MirrorP", {"position": v(0, -90) * mm});
            skArc(sketch, "E92.MirrorCS", {"start": v(15, -120) * mm, "mid": v(0, -135) * mm, "end": v(-15, -120) * mm});
            skLineSegment(sketch, "E93.MirrorCS", {"start": v(-33, -90) * mm, "end": v(-15, -108) * mm});
            skLineSegment(sketch, "E94.MirrorCS", {"start": v(-33, -90) * mm, "end": v(33, -90) * mm});
            skLineSegment(sketch, "E95.MirrorCS", {"start": v(15, -108) * mm, "end": v(33, -90) * mm});
            skCircle(sketch, "E96.MirrorC", {"center": v(0, -120) * mm, "radius": 6 * mm});
            skSolve(sketch);
        }
        {
            var Q0;
            Q0=makeQuery(id+"F16.imprint","IMPRINT",FACE,{"disambiguationData":[TD([[makeQuery(id+"F16.imprint","IMPRINT",EDGE,{"derivedFrom":sQuery(id+"F16.wireOp",EDGE,"E89.MirrorCS")}),1.0]])]});
            var Q1;
            Q1=makeQuery(id+"F16.imprint","IMPRINT",FACE,{"disambiguationData":[TD([[makeQuery(id+"F16.imprint","IMPRINT",EDGE,{"derivedFrom":sQuery(id+"F16.wireOp",EDGE,"E80")}),-1.0]])]});
            var Q2;
            {var subQ4=sQuery(id+"F16.wireOp",EDGE,"E84");Q2=makeQuery(id+"F16.imprint","IMPRINT",FACE,{"disambiguationData":[TD([[makeQuery(id+"F16.imprint","IMPRINT",EDGE,{"derivedFrom":subQ4}),-1.0]])]});}
            var Q3;
            Q3=makeQuery(id+"F2.opExtrude","CAP_FACE",FACE,{"disambiguationData":[OSD([sQuery(id+"F0.wireOp",EDGE,"E12"),sQuery(id+"F0.wireOp",EDGE,"E13"),sQuery(id+"F0.wireOp",EDGE,"E14"),sQuery(id+"F0.wireOp",EDGE,"E15"),sQuery(id+"F0.wireOp",EDGE,"E17.filletArc"),sQuery(id+"F0.wireOp",EDGE,"E18.filletArc"),sQuery(id+"F0.wireOp",EDGE,"E19.filletArc"),sQuery(id+"F0.wireOp",EDGE,"E20.filletArc"),sQuery(id+"F0.wireOp",EDGE,"E25.0"),sQuery(id+"F0.wireOp",EDGE,"E25.1"),sQuery(id+"F0.wireOp",EDGE,"E25.2"),sQuery(id+"F0.wireOp",EDGE,"E25.3"),sQuery(id+"F0.wireOp",EDGE,"E25.4"),sQuery(id+"F0.wireOp",EDGE,"E25.5"),sQuery(id+"F0.wireOp",EDGE,"E25.6"),sQuery(id+"F0.wireOp",EDGE,"E25.7")])],"isStart":false});
            extrude(context, id + "F17", {"entities" : qUnion([Q0, Q1, Q2]), "endBound" : BoundingType.UP_TO_SURFACE, "depth" : 25 * mm, "endBoundEntityFace" : qUnion([Q3]), "offsetDistance" : 25 * mm});
        }
    });
